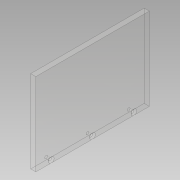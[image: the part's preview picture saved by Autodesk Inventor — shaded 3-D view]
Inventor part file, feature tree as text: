
AUTODESK INVENTOR PART (.ipt)
format: ipt  version: 2019 (Build 230136000, 136)  size: 92,672 bytes
history: native  units: mm
features: sketch x2, other x1, extrude x1, hole x1
ambient origin geometry x8: Origin, YZ Plane, XZ Plane, XY Plane, X Axis, Y Axis, Z Axis, Center Point
bodies: Body1 (feature_tree)
feature tree (5):
  other  "Sólido1"
  extrude  "Extrusión1"  Depth=220.0mm
  hole  "Agujero1"  [1 undecoded]
  sketch  "Boceto1"  dims[d0=160.0mm d1=220.0mm]
  sketch  "Boceto2"  dims[d2=10.0mm d3=0.0mm d8=5.5mm d9=6.0mm d10=11.0mm d11=2.0mm d12=90.0deg d13=20.0mm d14=20.594885mm]
note: 1 required parameter value undecoded (feature->parameter linkage not recoverable at this tier; creation-order binding heuristic only, values carry confidence <= 0.55)
